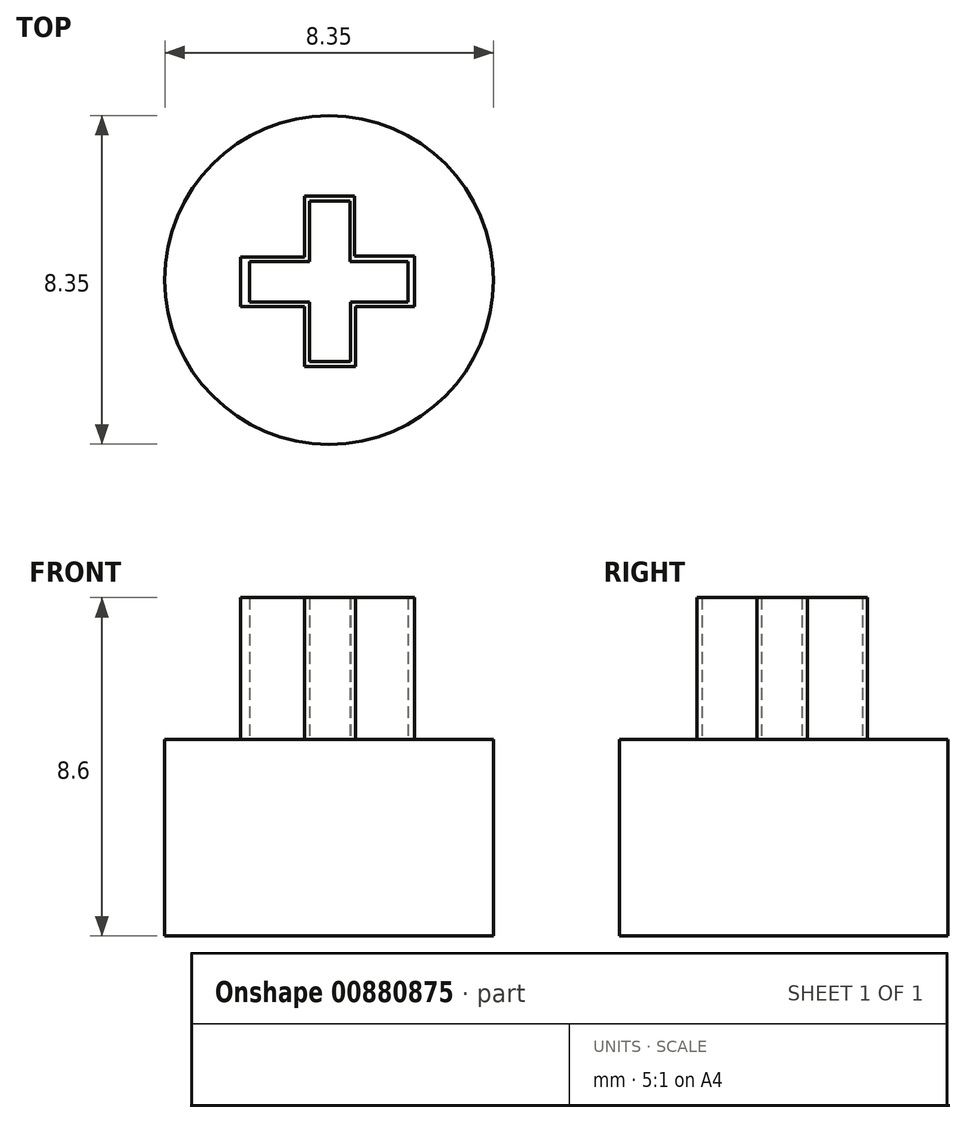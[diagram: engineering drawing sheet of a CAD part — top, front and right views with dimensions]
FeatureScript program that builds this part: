
annotation { "Feature Type Name" : "Feature", "Feature Type Description" : "" }
export const myFeature = defineFeature(function(context is Context, id is Id, definition is map)
    precondition{}
    {
        {
            var Q0;
            Q0=qCreatedBy(makeId("Top.planeOp"),FACE);
            var sketch = newSketch(context, id + "F0", { "sketchPlane" : qUnion([Q0])});
            skArc(sketch, "E0", {"start": v(-16.33, -3.7) * mm, "mid": v(-16.04, -4.5) * mm, "end": v(-15.3, -4.9) * mm});
            skLineSegment(sketch, "E1", {"start": v(-15.3, -4.9) * mm, "end": v(0.7, -4.9) * mm});
            skArc(sketch, "E2", {"start": v(0.7, -4.9) * mm, "mid": v(1.53, -4.58) * mm, "end": v(1.97, -3.81) * mm});
            skLineSegment(sketch, "E3", {"start": v(1.97, -3.81) * mm, "end": v(1.97, 12.15) * mm});
            skArc(sketch, "E4", {"start": v(1.97, 12.15) * mm, "mid": v(1.64, 13) * mm, "end": v(0.83, 13.4) * mm});
            skLineSegment(sketch, "E5", {"start": v(0.83, 13.4) * mm, "end": v(-15.1, 13.4) * mm});
            skArc(sketch, "E6", {"start": v(-15.1, 13.4) * mm, "mid": v(-15.95, 13.07) * mm, "end": v(-16.33, 12.24) * mm});
            skLineSegment(sketch, "E7", {"start": v(-16.33, -3.7) * mm, "end": v(-16.33, 12.24) * mm});
            skCircle(sketch, "E8", {"center": v(-7.17, 4.25) * mm, "radius": 2.79 * mm});
            skPoint(sketch, "E8.first.point", {"position": v(-9.1, 6.26) * mm});
            skPoint(sketch, "E8.second.point", {"position": v(-5.32, 2.17) * mm});
            skPoint(sketch, "E8.third.point", {"position": v(-4.95, 5.93) * mm});
            skLineSegment(sketch, "E9", {"start": v(-7.68, 6.22) * mm, "end": v(-7.68, 4.7) * mm});
            skLineSegment(sketch, "E10", {"start": v(-7.68, 4.7) * mm, "end": v(-9.2, 4.7) * mm});
            skLineSegment(sketch, "E11", {"start": v(-9.2, 4.7) * mm, "end": v(-9.2, 3.68) * mm});
            skLineSegment(sketch, "E12", {"start": v(-9.2, 3.68) * mm, "end": v(-7.68, 3.68) * mm});
            skLineSegment(sketch, "E13", {"start": v(-7.68, 3.68) * mm, "end": v(-7.68, 2.17) * mm});
            skLineSegment(sketch, "E14", {"start": v(-7.68, 2.17) * mm, "end": v(-6.64, 2.17) * mm});
            skLineSegment(sketch, "E15", {"start": v(-6.64, 2.17) * mm, "end": v(-6.64, 3.68) * mm});
            skLineSegment(sketch, "E16", {"start": v(-6.64, 3.68) * mm, "end": v(-5.17, 3.68) * mm});
            skLineSegment(sketch, "E17", {"start": v(-5.17, 3.68) * mm, "end": v(-5.17, 4.7) * mm});
            skLineSegment(sketch, "E18", {"start": v(-5.17, 4.7) * mm, "end": v(-6.64, 4.7) * mm});
            skLineSegment(sketch, "E19", {"start": v(-6.64, 4.7) * mm, "end": v(-6.64, 6.24) * mm});
            skLineSegment(sketch, "E20", {"start": v(-6.64, 6.24) * mm, "end": v(-7.68, 6.24) * mm});
            skLineSegment(sketch, "E21", {"start": v(-7.68, 6.24) * mm, "end": v(-7.68, 6.22) * mm});
            skLineSegment(sketch, "E22", {"start": v(-7.8, 3.4) * mm, "end": v(-7.8, 2.04) * mm});
            skLineSegment(sketch, "E23", {"start": v(-7.8, 2.04) * mm, "end": v(-6.51, 2.04) * mm});
            skLineSegment(sketch, "E24", {"start": v(-6.51, 2.04) * mm, "end": v(-6.51, 3.57) * mm});
            skLineSegment(sketch, "E25", {"start": v(-6.51, 3.57) * mm, "end": v(-5, 3.57) * mm});
            skLineSegment(sketch, "E26", {"start": v(-5, 3.57) * mm, "end": v(-5, 4.85) * mm});
            skLineSegment(sketch, "E27", {"start": v(-5, 4.85) * mm, "end": v(-6.53, 4.85) * mm});
            skLineSegment(sketch, "E28", {"start": v(-6.53, 4.85) * mm, "end": v(-6.53, 6.37) * mm});
            skLineSegment(sketch, "E29", {"start": v(-6.53, 6.37) * mm, "end": v(-7.8, 6.37) * mm});
            skLineSegment(sketch, "E30", {"start": v(-7.8, 6.37) * mm, "end": v(-7.8, 4.82) * mm});
            skLineSegment(sketch, "E31", {"start": v(-7.8, 4.82) * mm, "end": v(-9.42, 4.82) * mm});
            skLineSegment(sketch, "E32", {"start": v(-9.42, 4.82) * mm, "end": v(-9.42, 3.57) * mm});
            skLineSegment(sketch, "E33", {"start": v(-9.42, 3.57) * mm, "end": v(-7.8, 3.57) * mm});
            skLineSegment(sketch, "E34", {"start": v(-7.8, 3.4) * mm, "end": v(-7.8, 3.57) * mm});
            skSolve(sketch);
        }
        {
            var Q0;
            Q0=makeQuery(id+"F0.imprint","IMPRINT",FACE,{"disambiguationData":[TD([[makeQuery(id+"F0.imprint","IMPRINT",EDGE,{"derivedFrom":sQuery(id+"F0.wireOp",EDGE,"E9")}),-1.0]])]});
            extrude(context, id + "F1", {"entities" : qUnion([Q0]), "depth" : 3.6 * mm, "offsetDistance" : 25 * mm});
        }
        {
            var Q0;
            Q0=makeQuery(id+"F1.opExtrude","CAP_FACE",FACE,{"disambiguationData":[OSD([sQuery(id+"F0.wireOp",EDGE,"E9"),sQuery(id+"F0.wireOp",EDGE,"E10"),sQuery(id+"F0.wireOp",EDGE,"E11"),sQuery(id+"F0.wireOp",EDGE,"E12"),sQuery(id+"F0.wireOp",EDGE,"E13"),sQuery(id+"F0.wireOp",EDGE,"E14"),sQuery(id+"F0.wireOp",EDGE,"E15"),sQuery(id+"F0.wireOp",EDGE,"E16"),sQuery(id+"F0.wireOp",EDGE,"E17"),sQuery(id+"F0.wireOp",EDGE,"E18"),sQuery(id+"F0.wireOp",EDGE,"E19"),sQuery(id+"F0.wireOp",EDGE,"E20"),sQuery(id+"F0.wireOp",EDGE,"E21"),sQuery(id+"F0.wireOp",EDGE,"E22"),sQuery(id+"F0.wireOp",EDGE,"E23"),sQuery(id+"F0.wireOp",EDGE,"E24"),sQuery(id+"F0.wireOp",EDGE,"E25"),sQuery(id+"F0.wireOp",EDGE,"E26"),sQuery(id+"F0.wireOp",EDGE,"E27"),sQuery(id+"F0.wireOp",EDGE,"E28"),sQuery(id+"F0.wireOp",EDGE,"E29"),sQuery(id+"F0.wireOp",EDGE,"E30"),sQuery(id+"F0.wireOp",EDGE,"E31"),sQuery(id+"F0.wireOp",EDGE,"E32"),sQuery(id+"F0.wireOp",EDGE,"E33"),sQuery(id+"F0.wireOp",EDGE,"E34")])],"isStart":true});
            var sketch = newSketch(context, id + "F2", { "sketchPlane" : qUnion([Q0])});
            skCircle(sketch, "E35", {"center": v(-7.18, -4.24) * mm, "radius": 4.18 * mm});
            skSolve(sketch);
        }
        {
            var Q0;
            Q0 = qSketchRegion(id + "F2", true);
            extrude(context, id + "F3", {"entities" : qUnion([Q0]), "operationType" : NewBodyOperationType.ADD, "depth" : 5 * mm, "offsetDistance" : 25 * mm});
        }
    });
